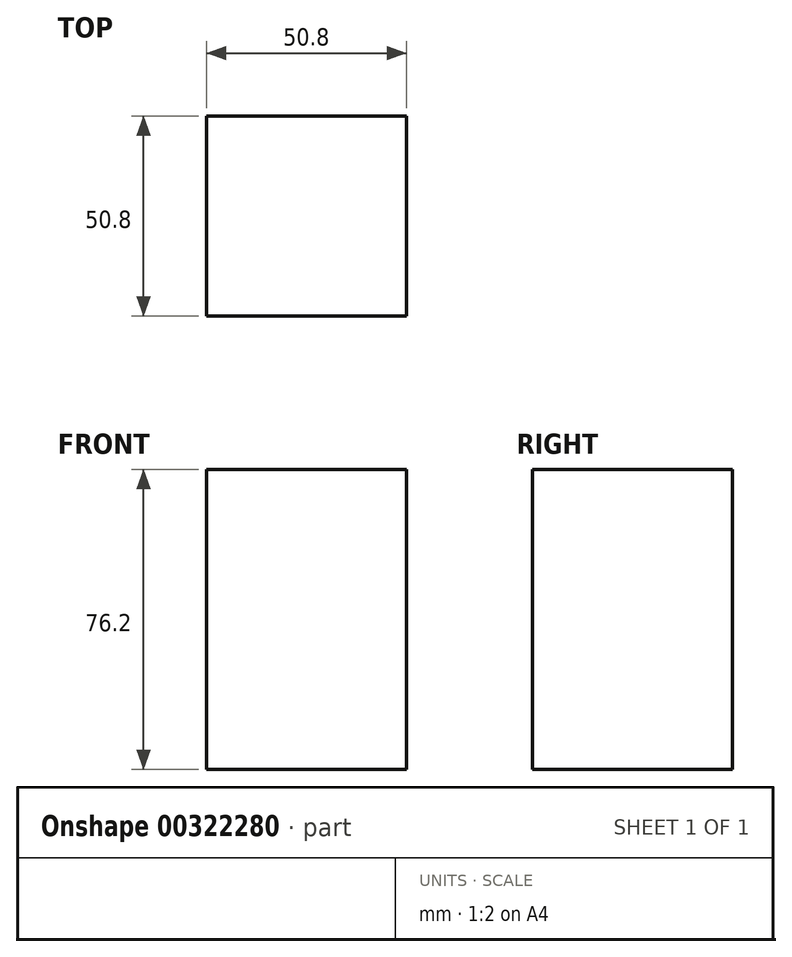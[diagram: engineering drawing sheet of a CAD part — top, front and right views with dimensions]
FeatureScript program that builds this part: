
annotation { "Feature Type Name" : "Feature", "Feature Type Description" : "" }
export const myFeature = defineFeature(function(context is Context, id is Id, definition is map)
    precondition{}
    {
        {
            var Q0;
            Q0=qCreatedBy(makeId("Top.planeOp"),FACE);
            var sketch = newSketch(context, id + "F0", { "sketchPlane" : qUnion([Q0])});
            skLineSegment(sketch, "E0.bottom", {"start": v(-50.8, 0) * mm, "end": v(0, 0) * mm});
            skLineSegment(sketch, "E0.top", {"start": v(-50.8, -50.8) * mm, "end": v(0, -50.8) * mm});
            skLineSegment(sketch, "E0.left", {"start": v(-50.8, 0) * mm, "end": v(-50.8, -50.8) * mm});
            skLineSegment(sketch, "E0.right", {"start": v(0, 0) * mm, "end": v(0, -50.8) * mm});
            skSolve(sketch);
        }
        {
            var Q0;
            Q0 = qSketchRegion(id + "F0", true);
            extrude(context, id + "F1", {"entities" : qUnion([Q0]), "depth" : 76.2 * mm});
        }
    });
